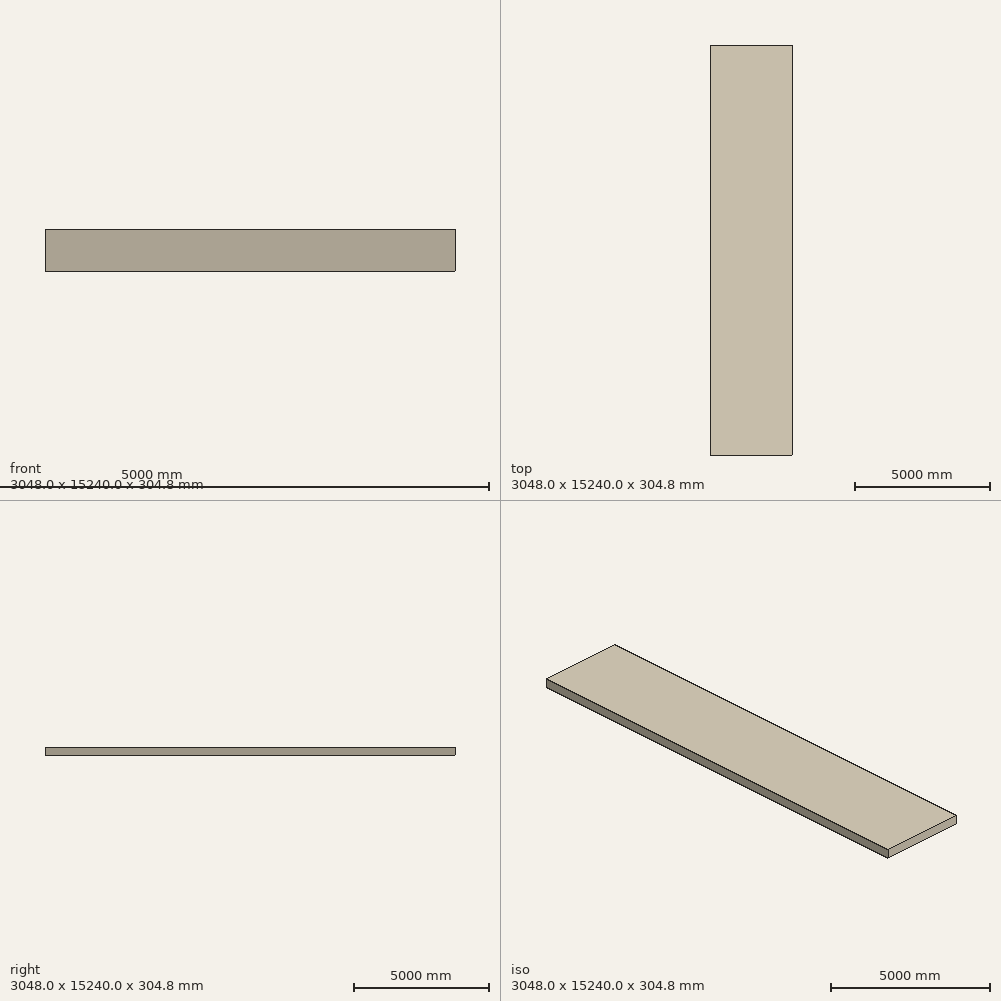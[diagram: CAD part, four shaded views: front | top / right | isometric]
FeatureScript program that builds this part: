
annotation { "Feature Type Name" : "Feature", "Feature Type Description" : "" }
export const myFeature = defineFeature(function(context is Context, id is Id, definition is map)
    precondition{}
    {
        {
            var Q0;
            Q0=qCreatedBy(makeId("Front.planeOp"),FACE);
            var sketch = newSketch(context, id + "F0", { "sketchPlane" : qUnion([Q0])});
            skLineSegment(sketch, "E0.bottom", {"start": v(-1067.89, 116.27) * mm, "end": v(1980.11, 116.27) * mm});
            skLineSegment(sketch, "E0.top", {"start": v(-1067.89, -188.53) * mm, "end": v(1980.11, -188.53) * mm});
            skLineSegment(sketch, "E0.left", {"start": v(-1067.89, 116.27) * mm, "end": v(-1067.89, -188.53) * mm});
            skLineSegment(sketch, "E0.right", {"start": v(1980.11, 116.27) * mm, "end": v(1980.11, -188.53) * mm});
            skSolve(sketch);
        }
        {
            var Q0;
            Q0 = qSketchRegion(id + "F0", true);
            extrude(context, id + "F1", {"entities" : qUnion([Q0]), "oppositeDirection" : true, "depth" : 15240 * mm, "offsetDistance" : 25.4 * mm});
        }
    });
